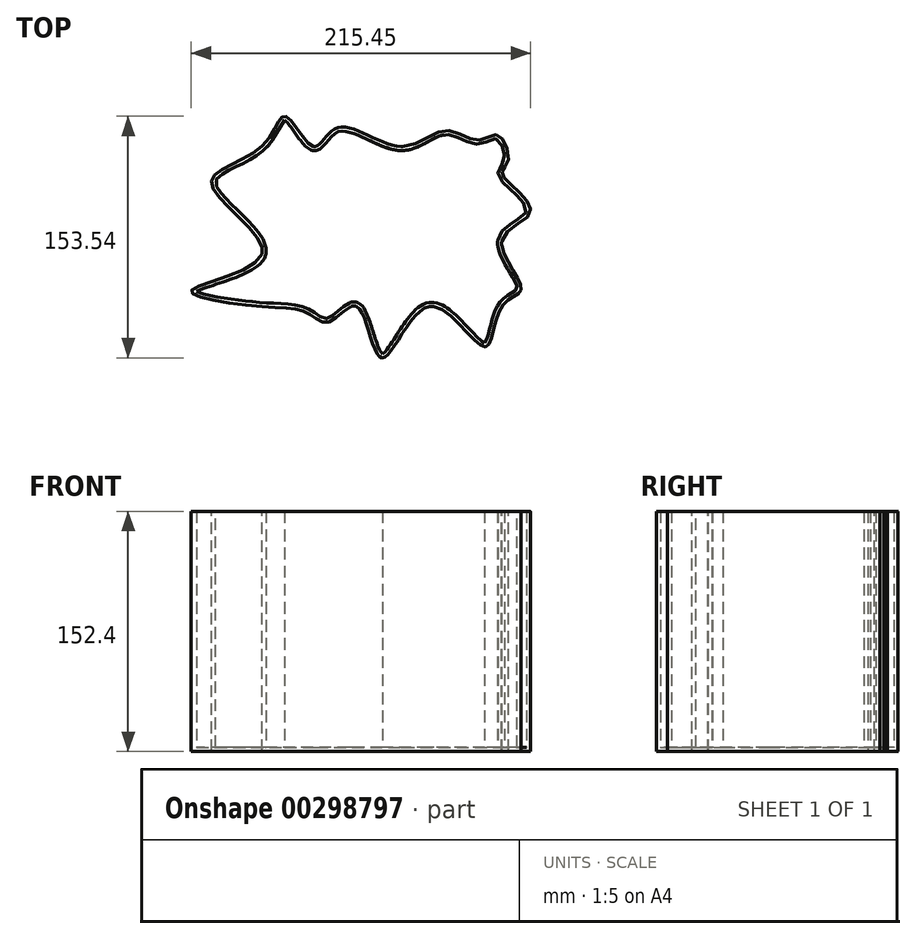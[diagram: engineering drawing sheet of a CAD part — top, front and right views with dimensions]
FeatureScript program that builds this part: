
annotation { "Feature Type Name" : "Feature", "Feature Type Description" : "" }
export const myFeature = defineFeature(function(context is Context, id is Id, definition is map)
    precondition{}
    {
        {
            var Q0;
            Q0=qCreatedBy(makeId("Top.planeOp"),FACE);
            var sketch = newSketch(context, id + "F0", { "sketchPlane" : qUnion([Q0])});
            skLineSegment(sketch, "E0.bottom", {"start": v(-43.38, 50.8) * mm, "end": v(-42.23, 50.8) * mm});
            skLineSegment(sketch, "E0.top", {"start": v(-19.67, -50.8) * mm, "end": v(-15.94, -50.8) * mm});
            skLineSegment(sketch, "E0.left", {"start": v(-76.2, -13.17) * mm, "end": v(-76.2, -17.44) * mm});
            skLineSegment(sketch, "E0.right", {"start": v(76.2, -9.14) * mm, "end": v(76.2, -12.24) * mm});
            skPoint(sketch, "E0.middle", {"position": v(0, 0) * mm});
            skFitSpline(sketch, "E1", {"points": [v(-43.38, 50.8) * mm, v(-28.3, 62.74) * mm, v(12.23, 50.8) * mm, v(40.23, 60.99) * mm, v(61.23, 54.86) * mm, v(73.77, 58.07) * mm, v(80.2, 41.74) * mm, v(76.2, 34.45) * mm, v(86.9, 22.2) * mm, v(93.75, 7.9) * mm, v(76.2, -9.14) * mm, v(88.5, -39.29) * mm, v(76.2, -50.8) * mm, v(65.34, -76.43) * mm, v(30.38, -50.8) * mm, v(0, -83.42) * mm, v(-15.94, -50.8) * mm, v(-33.42, -60.7) * mm, v(-46.97, -55.02) * mm, v(-76.2, -50.8) * mm, v(-120.82, -40.6) * mm, v(-76.2, -17.44) * mm, v(-108.15, 27.14) * mm, v(-76.2, 50.8) * mm, v(-60.95, 69.96) * mm, v(-43.38, 50.8) * mm]});
            skPoint(sketch, "E2.visualSharp", {"position": v(76.2, 50.8) * mm});
            skLineSegment(sketch, "E3.trimOffspring", {"start": v(12.23, 50.8) * mm, "end": v(13.1, 50.8) * mm});
            skLineSegment(sketch, "E4.trimOffspring", {"start": v(30.38, -50.8) * mm, "end": v(32.91, -50.8) * mm});
            skSolve(sketch);
        }
        {
            var Q0;
            {var subQ0=sQuery(id+"F0.wireOp",EDGE,"E1");var subQ12=sQuery(id+"F0.wireOp",EDGE,"E0.bottom");var subQ13=makeQuery(id+"F0.imprint","INTERSECT",VERTEX,{"disambiguationData":[OD(0.0)],"derivedFrom":[subQ12,subQ0]});Q0=makeQuery(id+"F0.imprint","IMPRINT",FACE,{"disambiguationData":[TD([[makeQuery(id+"F0.imprint","IMPRINT",EDGE,{"disambiguationData":[TD([[subQ13,-1.0]])],"derivedFrom":subQ0}),-1.0]])]});}
            extrude(context, id + "F1", {"entities" : qUnion([Q0]), "depth" : 152.4 * mm});
        }
        {
            var Q0;
            Q0=makeQuery(id+"F1.opExtrude","CAP_FACE",FACE,{"disambiguationData":[OSD([sQuery(id+"F0.wireOp",EDGE,"E1")])],"isStart":false});
            shell(context, id + "F2", {"entities" : qUnion([Q0]), "thickness" : 2.54 * mm});
        }
    });
